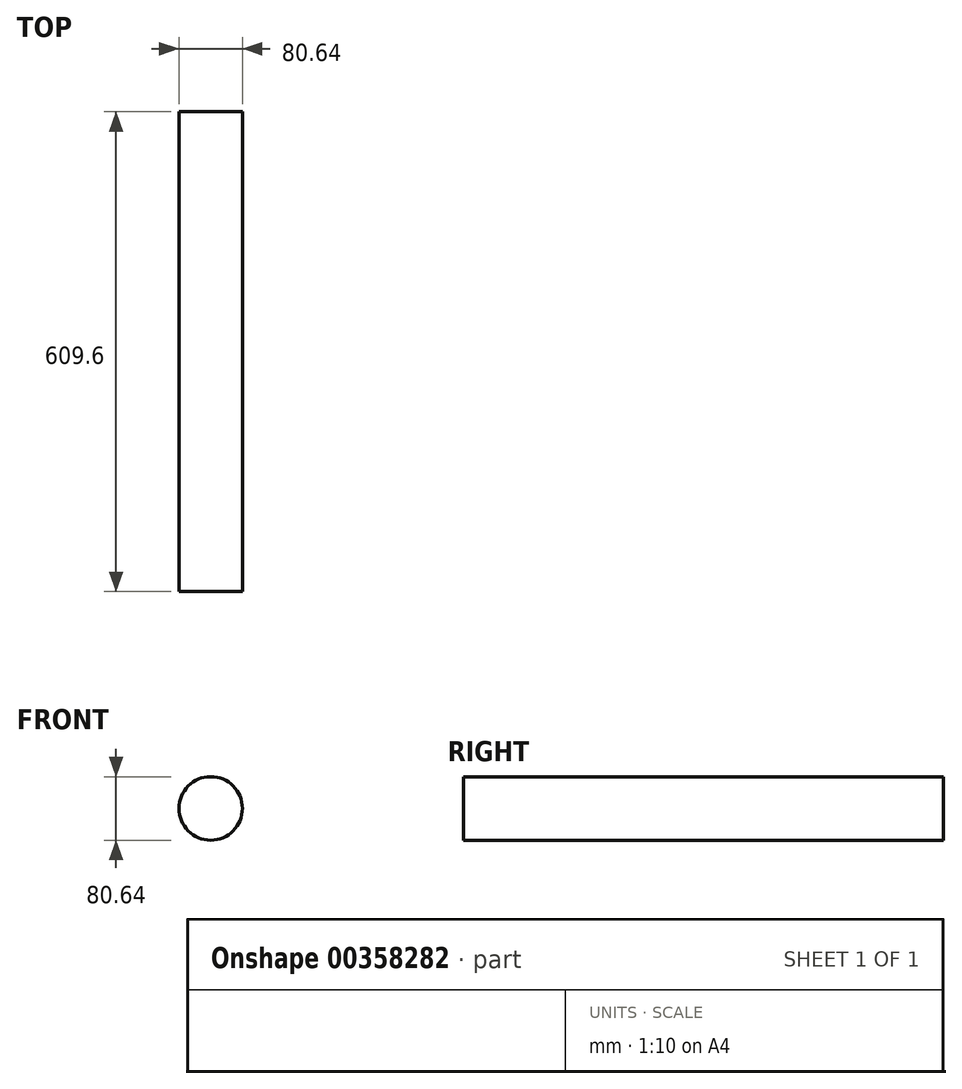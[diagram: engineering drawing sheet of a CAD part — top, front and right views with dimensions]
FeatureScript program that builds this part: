
annotation { "Feature Type Name" : "Feature", "Feature Type Description" : "" }
export const myFeature = defineFeature(function(context is Context, id is Id, definition is map)
    precondition{}
    {
        {
            var Q0;
            Q0=qCreatedBy(makeId("Front.planeOp"),FACE);
            var sketch = newSketch(context, id + "F0", { "sketchPlane" : qUnion([Q0])});
            skCircle(sketch, "E0", {"center": v(0, 0) * mm, "radius": 40.32 * mm});
            skSolve(sketch);
        }
        {
            var Q0;
            Q0 = qSketchRegion(id + "F0", true);
            extrude(context, id + "F1", {"entities" : qUnion([Q0]), "depth" : 609.6 * mm});
        }
    });
